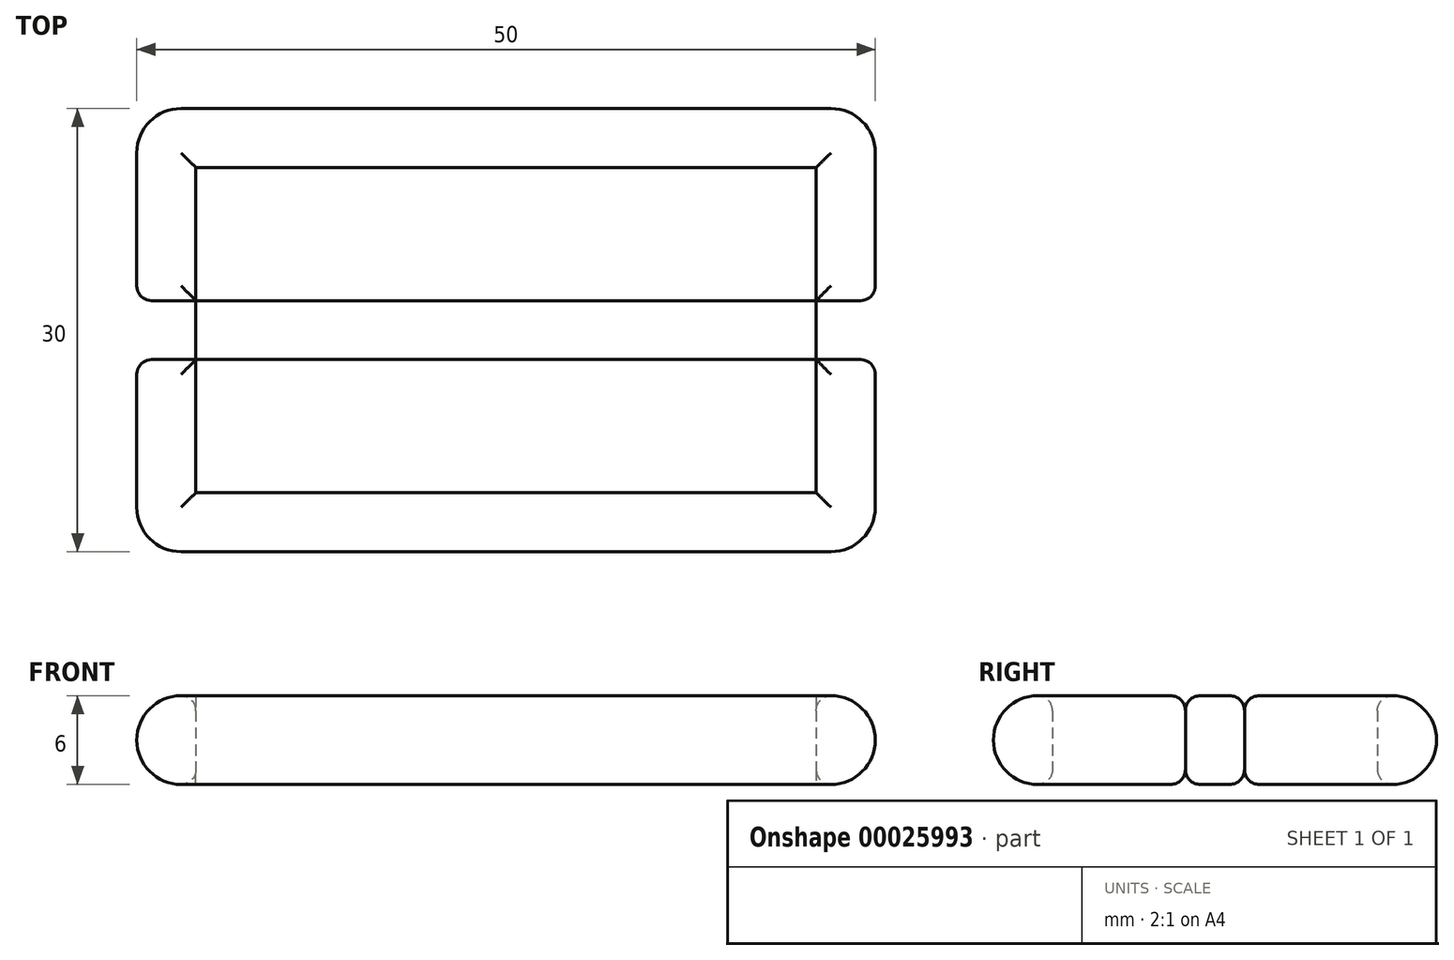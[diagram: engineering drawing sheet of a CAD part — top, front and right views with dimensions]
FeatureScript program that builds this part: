
annotation { "Feature Type Name" : "Feature", "Feature Type Description" : "" }
export const myFeature = defineFeature(function(context is Context, id is Id, definition is map)
    precondition{}
    {
        {
            var Q0;
            Q0=qCreatedBy(makeId("Top.planeOp"),FACE);
            cPlane(context, id + "F0", {"entities" : qUnion([Q0]), "cplaneType" : CPlaneType.OFFSET, "offset" : 3 * mm, "oppositeDirection" : true, "width" : 150 * mm, "height" : 150 * mm});
        }
        {
            var Q0;
            Q0=qCreatedBy(id+"F0.planeOp",FACE);
            var sketch = newSketch(context, id + "F1", { "sketchPlane" : qUnion([Q0])});
            skLineSegment(sketch, "E0.rect.bottom", {"start": v(25, 15) * mm, "end": v(-25, 15) * mm});
            skLineSegment(sketch, "E0.rect.top", {"start": v(25, -15) * mm, "end": v(-25, -15) * mm});
            skLineSegment(sketch, "E0.rect.left", {"start": v(25, 15) * mm, "end": v(25, -15) * mm});
            skLineSegment(sketch, "E0.rect.right", {"start": v(-25, 15) * mm, "end": v(-25, -15) * mm});
            skPoint(sketch, "E0.rect.middle", {"position": v(0, 0) * mm});
            skLineSegment(sketch, "E1.0", {"start": v(25, 11) * mm, "end": v(-25, 11) * mm});
            skLineSegment(sketch, "E2.0", {"start": v(25, -11) * mm, "end": v(-25, -11) * mm});
            skLineSegment(sketch, "E3.0", {"start": v(-21, 15) * mm, "end": v(-21, -15) * mm});
            skLineSegment(sketch, "E4.0", {"start": v(21, 15) * mm, "end": v(21, -15) * mm});
            skLineSegment(sketch, "E5.rect.bottom", {"start": v(-25, 2) * mm, "end": v(25, 2) * mm});
            skLineSegment(sketch, "E5.rect.top", {"start": v(-25, -2) * mm, "end": v(25, -2) * mm});
            skLineSegment(sketch, "E5.rect.left", {"start": v(-25, 2) * mm, "end": v(-25, -2) * mm});
            skLineSegment(sketch, "E5.rect.right", {"start": v(25, 2) * mm, "end": v(25, -2) * mm});
            skSolve(sketch);
        }
        {
            var Q0;
            {var subQ3=sQuery(id+"F1.wireOp",EDGE,"E0.rect.top");var subQ5=sQuery(id+"F1.wireOp",EDGE,"E3.0");var subQ7=makeQuery(id+"F1.imprint","INTERSECT",VERTEX,{"derivedFrom":[subQ3,subQ5]});Q0=makeQuery(id+"F1.imprint","IMPRINT",FACE,{"disambiguationData":[TD([[makeQuery(id+"F1.imprint","IMPRINT",EDGE,{"disambiguationData":[TD([[subQ7,1.0]])],"derivedFrom":subQ3}),-1.0]])]});}
            var Q1;
            {var subQ3=sQuery(id+"F1.wireOp",EDGE,"E0.rect.top");var subQ5=sQuery(id+"F1.wireOp",EDGE,"E0.rect.right");var subQ7=makeQuery(id+"F1.imprint","INTERSECT",VERTEX,{"derivedFrom":[subQ3,subQ5]});Q1=makeQuery(id+"F1.imprint","IMPRINT",FACE,{"disambiguationData":[TD([[makeQuery(id+"F1.imprint","IMPRINT",EDGE,{"disambiguationData":[TD([[subQ7,1.0]])],"derivedFrom":subQ3}),-1.0]])]});}
            var Q2;
            {var subQ3=sQuery(id+"F1.wireOp",EDGE,"E0.rect.right");var subQ5=sQuery(id+"F1.wireOp",EDGE,"E2.0");var subQ7=makeQuery(id+"F1.imprint","INTERSECT",VERTEX,{"derivedFrom":[subQ3,subQ5]});Q2=makeQuery(id+"F1.imprint","IMPRINT",FACE,{"disambiguationData":[TD([[makeQuery(id+"F1.imprint","IMPRINT",EDGE,{"disambiguationData":[TD([[subQ7,1.0]])],"derivedFrom":subQ5}),-1.0]])]});}
            var Q3;
            {var subQ0=sQuery(id+"F1.wireOp",EDGE,"E5.rect.left");Q3=makeQuery(id+"F1.imprint","IMPRINT",FACE,{"disambiguationData":[TD([[makeQuery(id+"F1.imprint","IMPRINT",EDGE,{"derivedFrom":subQ0}),1.0]])]});}
            var Q4;
            {var subQ3=sQuery(id+"F1.wireOp",EDGE,"E0.rect.right");var subQ5=sQuery(id+"F1.wireOp",EDGE,"E1.0");var subQ7=makeQuery(id+"F1.imprint","INTERSECT",VERTEX,{"derivedFrom":[subQ3,subQ5]});Q4=makeQuery(id+"F1.imprint","IMPRINT",FACE,{"disambiguationData":[TD([[makeQuery(id+"F1.imprint","IMPRINT",EDGE,{"disambiguationData":[TD([[subQ7,1.0]])],"derivedFrom":subQ5}),1.0]])]});}
            var Q5;
            {var subQ3=sQuery(id+"F1.wireOp",EDGE,"E0.rect.bottom");var subQ5=sQuery(id+"F1.wireOp",EDGE,"E0.rect.right");var subQ7=makeQuery(id+"F1.imprint","INTERSECT",VERTEX,{"derivedFrom":[subQ3,subQ5]});Q5=makeQuery(id+"F1.imprint","IMPRINT",FACE,{"disambiguationData":[TD([[makeQuery(id+"F1.imprint","IMPRINT",EDGE,{"disambiguationData":[TD([[subQ7,1.0]])],"derivedFrom":subQ3}),1.0]])]});}
            var Q6;
            {var subQ3=sQuery(id+"F1.wireOp",EDGE,"E0.rect.bottom");var subQ5=sQuery(id+"F1.wireOp",EDGE,"E3.0");var subQ7=makeQuery(id+"F1.imprint","INTERSECT",VERTEX,{"derivedFrom":[subQ3,subQ5]});Q6=makeQuery(id+"F1.imprint","IMPRINT",FACE,{"disambiguationData":[TD([[makeQuery(id+"F1.imprint","IMPRINT",EDGE,{"disambiguationData":[TD([[subQ7,1.0]])],"derivedFrom":subQ3}),1.0]])]});}
            var Q7;
            {var subQ3=sQuery(id+"F1.wireOp",EDGE,"E0.rect.bottom");var subQ5=sQuery(id+"F1.wireOp",EDGE,"E0.rect.left");var subQ7=makeQuery(id+"F1.imprint","INTERSECT",VERTEX,{"derivedFrom":[subQ3,subQ5]});Q7=makeQuery(id+"F1.imprint","IMPRINT",FACE,{"disambiguationData":[TD([[makeQuery(id+"F1.imprint","IMPRINT",EDGE,{"disambiguationData":[TD([[subQ7,-1.0]])],"derivedFrom":subQ3}),1.0]])]});}
            var Q8;
            {var subQ0=sQuery(id+"F1.wireOp",EDGE,"E5.rect.right");Q8=makeQuery(id+"F1.imprint","IMPRINT",FACE,{"disambiguationData":[TD([[makeQuery(id+"F1.imprint","IMPRINT",EDGE,{"derivedFrom":subQ0}),-1.0]])]});}
            var Q9;
            {var subQ3=sQuery(id+"F1.wireOp",EDGE,"E0.rect.left");var subQ5=sQuery(id+"F1.wireOp",EDGE,"E1.0");var subQ7=makeQuery(id+"F1.imprint","INTERSECT",VERTEX,{"derivedFrom":[subQ3,subQ5]});Q9=makeQuery(id+"F1.imprint","IMPRINT",FACE,{"disambiguationData":[TD([[makeQuery(id+"F1.imprint","IMPRINT",EDGE,{"disambiguationData":[TD([[subQ7,-1.0]])],"derivedFrom":subQ5}),1.0]])]});}
            var Q10;
            {var subQ3=sQuery(id+"F1.wireOp",EDGE,"E0.rect.left");var subQ5=sQuery(id+"F1.wireOp",EDGE,"E2.0");var subQ7=makeQuery(id+"F1.imprint","INTERSECT",VERTEX,{"derivedFrom":[subQ3,subQ5]});Q10=makeQuery(id+"F1.imprint","IMPRINT",FACE,{"disambiguationData":[TD([[makeQuery(id+"F1.imprint","IMPRINT",EDGE,{"disambiguationData":[TD([[subQ7,-1.0]])],"derivedFrom":subQ5}),-1.0]])]});}
            var Q11;
            {var subQ3=sQuery(id+"F1.wireOp",EDGE,"E0.rect.top");var subQ5=sQuery(id+"F1.wireOp",EDGE,"E0.rect.left");var subQ7=makeQuery(id+"F1.imprint","INTERSECT",VERTEX,{"derivedFrom":[subQ3,subQ5]});Q11=makeQuery(id+"F1.imprint","IMPRINT",FACE,{"disambiguationData":[TD([[makeQuery(id+"F1.imprint","IMPRINT",EDGE,{"disambiguationData":[TD([[subQ7,-1.0]])],"derivedFrom":subQ3}),-1.0]])]});}
            var Q12;
            {var subQ0=sQuery(id+"F1.wireOp",EDGE,"E5.rect.bottom");var subQ3=sQuery(id+"F1.wireOp",EDGE,"E3.0");var subQ4=makeQuery(id+"F1.imprint","INTERSECT",VERTEX,{"derivedFrom":[subQ3,subQ0]});Q12=makeQuery(id+"F1.imprint","IMPRINT",FACE,{"disambiguationData":[TD([[makeQuery(id+"F1.imprint","IMPRINT",EDGE,{"disambiguationData":[TD([[subQ4,-1.0]])],"derivedFrom":subQ3}),1.0]])]});}
            extrude(context, id + "F2", {"entities" : qUnion([Q0, Q1, Q2, Q3, Q4, Q5, Q6, Q7, Q8, Q9, Q10, Q11, Q12]), "depth" : 6 * mm});
        }
        {
            var Q0;
            Q0=makeQuery(id+"F2.opExtrude","SWEPT_EDGE",EDGE,{"disambiguationData":[OSD([sQuery(id+"F1.wireOp",EDGE,"E0.rect.top"),sQuery(id+"F1.wireOp",EDGE,"E0.rect.left")])]});
            var Q1;
            Q1=makeQuery(id+"F2.opExtrude","SWEPT_EDGE",EDGE,{"disambiguationData":[OSD([sQuery(id+"F1.wireOp",EDGE,"E0.rect.bottom"),sQuery(id+"F1.wireOp",EDGE,"E0.rect.left")])]});
            var Q2;
            Q2=makeQuery(id+"F2.opExtrude","SWEPT_EDGE",EDGE,{"disambiguationData":[OSD([sQuery(id+"F1.wireOp",EDGE,"E0.rect.top"),sQuery(id+"F1.wireOp",EDGE,"E0.rect.right")])]});
            var Q3;
            Q3=makeQuery(id+"F2.opExtrude","SWEPT_EDGE",EDGE,{"disambiguationData":[OSD([sQuery(id+"F1.wireOp",EDGE,"E0.rect.bottom"),sQuery(id+"F1.wireOp",EDGE,"E0.rect.right")])]});
            var Q4;
            Q4=makeQuery(id+"F2.opExtrude","CAP_EDGE",EDGE,{"disambiguationData":[OSD([sQuery(id+"F1.wireOp",EDGE,"E0.rect.top")])],"isStart":false});
            var Q5;
            Q5=makeQuery(id+"F2.opExtrude","CAP_EDGE",EDGE,{"disambiguationData":[OSD([sQuery(id+"F1.wireOp",EDGE,"E0.rect.left"),sQuery(id+"F1.wireOp",EDGE,"E5.rect.right")])],"isStart":false});
            var Q6;
            Q6=makeQuery(id+"F2.opExtrude","CAP_EDGE",EDGE,{"disambiguationData":[OSD([sQuery(id+"F1.wireOp",EDGE,"E0.rect.bottom")])],"isStart":false});
            var Q7;
            Q7=makeQuery(id+"F2.opExtrude","CAP_EDGE",EDGE,{"disambiguationData":[OSD([sQuery(id+"F1.wireOp",EDGE,"E0.rect.right"),sQuery(id+"F1.wireOp",EDGE,"E5.rect.left")])],"isStart":false});
            var Q8;
            Q8=makeQuery(id+"F2.opExtrude","CAP_EDGE",EDGE,{"disambiguationData":[OSD([sQuery(id+"F1.wireOp",EDGE,"E0.rect.left"),sQuery(id+"F1.wireOp",EDGE,"E5.rect.right")])],"isStart":true});
            var Q9;
            Q9=makeQuery(id+"F2.opExtrude","CAP_EDGE",EDGE,{"disambiguationData":[OSD([sQuery(id+"F1.wireOp",EDGE,"E0.rect.top")])],"isStart":true});
            var Q10;
            Q10=makeQuery(id+"F2.opExtrude","CAP_EDGE",EDGE,{"disambiguationData":[OSD([sQuery(id+"F1.wireOp",EDGE,"E0.rect.right"),sQuery(id+"F1.wireOp",EDGE,"E5.rect.left")])],"isStart":true});
            var Q11;
            Q11=makeQuery(id+"F2.opExtrude","CAP_EDGE",EDGE,{"disambiguationData":[OSD([sQuery(id+"F1.wireOp",EDGE,"E0.rect.bottom")])],"isStart":true});
            fillet(context, id + "F3", {"entities" : qUnion([Q0, Q1, Q2, Q3, Q4, Q5, Q6, Q7, Q8, Q9, Q10, Q11]), "radius" : 3 * mm, "tangentPropagation" : true, "allowEdgeOverflow" : false});
        }
        {
            var Q0;
            Q0=makeQuery(id+"F2.opExtrude","CAP_EDGE",EDGE,{"disambiguationData":[OSD([sQuery(id+"F1.wireOp",EDGE,"E1.0")])],"isStart":true});
            var Q1;
            Q1=makeQuery(id+"F2.opExtrude","CAP_EDGE",EDGE,{"disambiguationData":[OSD([sQuery(id+"F1.wireOp",EDGE,"E5.rect.bottom")])],"isStart":true});
            var Q2;
            {var subQ0=sQuery(id+"F1.wireOp",EDGE,"E4.0");Q2=makeQuery(id+"F2.opExtrude","CAP_EDGE",EDGE,{"disambiguationData":[OSD([subQ0]),TDD([makeQuery(id+"F1.imprint","IMPRINT",EDGE,{"disambiguationData":[TD([[makeQuery(id+"F1.imprint","INTERSECT",VERTEX,{"derivedFrom":[sQuery(id+"F1.wireOp",EDGE,"E1.0"),subQ0]}),-1.0]])],"derivedFrom":subQ0})])],"isStart":true});}
            var Q3;
            {var subQ0=sQuery(id+"F1.wireOp",EDGE,"E4.0");Q3=makeQuery(id+"F2.opExtrude","CAP_EDGE",EDGE,{"disambiguationData":[OSD([subQ0]),TDD([makeQuery(id+"F1.imprint","IMPRINT",EDGE,{"disambiguationData":[TD([[makeQuery(id+"F1.imprint","INTERSECT",VERTEX,{"derivedFrom":[sQuery(id+"F1.wireOp",EDGE,"E2.0"),subQ0]}),1.0]])],"derivedFrom":subQ0})])],"isStart":true});}
            var Q4;
            Q4=makeQuery(id+"F2.opExtrude","CAP_EDGE",EDGE,{"disambiguationData":[OSD([sQuery(id+"F1.wireOp",EDGE,"E5.rect.top")])],"isStart":true});
            var Q5;
            Q5=makeQuery(id+"F2.opExtrude","CAP_EDGE",EDGE,{"disambiguationData":[OSD([sQuery(id+"F1.wireOp",EDGE,"E2.0")])],"isStart":true});
            var Q6;
            {var subQ0=sQuery(id+"F1.wireOp",EDGE,"E3.0");Q6=makeQuery(id+"F2.opExtrude","CAP_EDGE",EDGE,{"disambiguationData":[OSD([subQ0]),TDD([makeQuery(id+"F1.imprint","IMPRINT",EDGE,{"disambiguationData":[TD([[makeQuery(id+"F1.imprint","INTERSECT",VERTEX,{"derivedFrom":[sQuery(id+"F1.wireOp",EDGE,"E2.0"),subQ0]}),1.0]])],"derivedFrom":subQ0})])],"isStart":true});}
            var Q7;
            {var subQ0=sQuery(id+"F1.wireOp",EDGE,"E3.0");Q7=makeQuery(id+"F2.opExtrude","CAP_EDGE",EDGE,{"disambiguationData":[OSD([subQ0]),TDD([makeQuery(id+"F1.imprint","IMPRINT",EDGE,{"disambiguationData":[TD([[makeQuery(id+"F1.imprint","INTERSECT",VERTEX,{"derivedFrom":[sQuery(id+"F1.wireOp",EDGE,"E1.0"),subQ0]}),-1.0]])],"derivedFrom":subQ0})])],"isStart":true});}
            var Q8;
            Q8=makeQuery(id+"F2.opExtrude","CAP_EDGE",EDGE,{"disambiguationData":[OSD([sQuery(id+"F1.wireOp",EDGE,"E1.0")])],"isStart":false});
            var Q9;
            {var subQ0=sQuery(id+"F1.wireOp",EDGE,"E4.0");Q9=makeQuery(id+"F2.opExtrude","CAP_EDGE",EDGE,{"disambiguationData":[OSD([subQ0]),TDD([makeQuery(id+"F1.imprint","IMPRINT",EDGE,{"disambiguationData":[TD([[makeQuery(id+"F1.imprint","INTERSECT",VERTEX,{"derivedFrom":[sQuery(id+"F1.wireOp",EDGE,"E1.0"),subQ0]}),-1.0]])],"derivedFrom":subQ0})])],"isStart":false});}
            var Q10;
            Q10=makeQuery(id+"F2.opExtrude","CAP_EDGE",EDGE,{"disambiguationData":[OSD([sQuery(id+"F1.wireOp",EDGE,"E5.rect.bottom")])],"isStart":false});
            var Q11;
            {var subQ0=sQuery(id+"F1.wireOp",EDGE,"E3.0");Q11=makeQuery(id+"F2.opExtrude","CAP_EDGE",EDGE,{"disambiguationData":[OSD([subQ0]),TDD([makeQuery(id+"F1.imprint","IMPRINT",EDGE,{"disambiguationData":[TD([[makeQuery(id+"F1.imprint","INTERSECT",VERTEX,{"derivedFrom":[sQuery(id+"F1.wireOp",EDGE,"E1.0"),subQ0]}),-1.0]])],"derivedFrom":subQ0})])],"isStart":false});}
            var Q12;
            {var subQ0=sQuery(id+"F1.wireOp",EDGE,"E3.0");Q12=makeQuery(id+"F2.opExtrude","CAP_EDGE",EDGE,{"disambiguationData":[OSD([subQ0]),TDD([makeQuery(id+"F1.imprint","IMPRINT",EDGE,{"disambiguationData":[TD([[makeQuery(id+"F1.imprint","INTERSECT",VERTEX,{"derivedFrom":[sQuery(id+"F1.wireOp",EDGE,"E2.0"),subQ0]}),1.0]])],"derivedFrom":subQ0})])],"isStart":false});}
            var Q13;
            Q13=makeQuery(id+"F2.opExtrude","CAP_EDGE",EDGE,{"disambiguationData":[OSD([sQuery(id+"F1.wireOp",EDGE,"E5.rect.top")])],"isStart":false});
            var Q14;
            {var subQ0=sQuery(id+"F1.wireOp",EDGE,"E4.0");Q14=makeQuery(id+"F2.opExtrude","CAP_EDGE",EDGE,{"disambiguationData":[OSD([subQ0]),TDD([makeQuery(id+"F1.imprint","IMPRINT",EDGE,{"disambiguationData":[TD([[makeQuery(id+"F1.imprint","INTERSECT",VERTEX,{"derivedFrom":[sQuery(id+"F1.wireOp",EDGE,"E2.0"),subQ0]}),1.0]])],"derivedFrom":subQ0})])],"isStart":false});}
            var Q15;
            Q15=makeQuery(id+"F2.opExtrude","CAP_EDGE",EDGE,{"disambiguationData":[OSD([sQuery(id+"F1.wireOp",EDGE,"E2.0")])],"isStart":false});
            fillet(context, id + "F4", {"entities" : qUnion([Q0, Q1, Q2, Q3, Q4, Q5, Q6, Q7, Q8, Q9, Q10, Q11, Q12, Q13, Q14, Q15]), "radius" : 1 * mm, "tangentPropagation" : true, "allowEdgeOverflow" : false});
        }
    });
